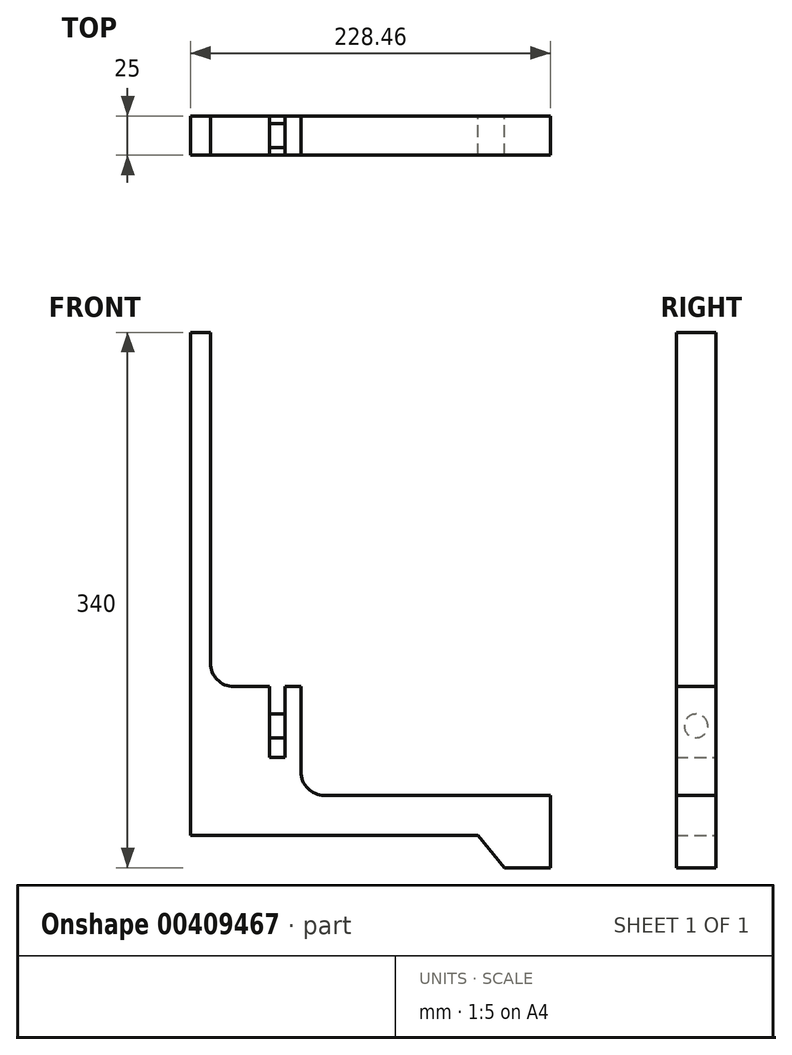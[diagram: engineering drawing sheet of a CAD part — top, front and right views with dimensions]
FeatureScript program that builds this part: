
annotation { "Feature Type Name" : "Feature", "Feature Type Description" : "" }
export const myFeature = defineFeature(function(context is Context, id is Id, definition is map)
    precondition{}
    {
        {
            var Q0;
            Q0=qCreatedBy(makeId("Front.planeOp"),FACE);
            var sketch = newSketch(context, id + "F0", { "sketchPlane" : qUnion([Q0])});
            skLineSegment(sketch, "E0", {"start": v(0, 20.37) * mm, "end": v(0, 340) * mm});
            skLineSegment(sketch, "E1", {"start": v(0, 340) * mm, "end": v(12.5, 340) * mm});
            skLineSegment(sketch, "E2", {"start": v(12.5, 340) * mm, "end": v(12.5, 130) * mm});
            skLineSegment(sketch, "E3", {"start": v(50, 70) * mm, "end": v(60, 70) * mm});
            skLineSegment(sketch, "E4", {"start": v(60, 70) * mm, "end": v(60, 100) * mm});
            skLineSegment(sketch, "E5", {"start": v(60, 100) * mm, "end": v(70, 100) * mm, "construction": true});
            skLineSegment(sketch, "E6", {"start": v(70, 100) * mm, "end": v(70, 60.94) * mm});
            skLineSegment(sketch, "E7", {"start": v(85, 45.94) * mm, "end": v(228.46, 45.94) * mm});
            skLineSegment(sketch, "E8", {"start": v(228.46, 45.94) * mm, "end": v(228.46, 0) * mm});
            skLineSegment(sketch, "E9", {"start": v(228.46, 0) * mm, "end": v(199.18, 0) * mm});
            skLineSegment(sketch, "E10", {"start": v(199.18, 0) * mm, "end": v(182.6, 20.37) * mm});
            skLineSegment(sketch, "E11", {"start": v(182.6, 20.37) * mm, "end": v(0, 20.37) * mm});
            skLineSegment(sketch, "E12", {"start": v(50, 100) * mm, "end": v(50, 70) * mm});
            skLineSegment(sketch, "E13", {"start": v(70, 100) * mm, "end": v(70, 115) * mm});
            skLineSegment(sketch, "E14", {"start": v(70, 115) * mm, "end": v(60, 115) * mm});
            skLineSegment(sketch, "E15", {"start": v(60, 115) * mm, "end": v(60, 100) * mm});
            skLineSegment(sketch, "E16", {"start": v(50, 100) * mm, "end": v(50, 115) * mm});
            skPoint(sketch, "E16.endSnap0", {"position": v(65, 115) * mm});
            skLineSegment(sketch, "E17", {"start": v(50, 115) * mm, "end": v(27.5, 115) * mm});
            skPoint(sketch, "E18.visualSharp", {"position": v(12.5, 115) * mm});
            skArc(sketch, "E18.filletArc", {"start": v(12.5, 130) * mm, "mid": v(16.9, 119.4) * mm, "end": v(27.5, 115) * mm});
            skPoint(sketch, "E19.visualSharp", {"position": v(70, 45.94) * mm});
            skArc(sketch, "E19.filletArc", {"start": v(70, 60.94) * mm, "mid": v(74.4, 50.33) * mm, "end": v(85, 45.94) * mm});
            skSolve(sketch);
        }
        {
            var Q0;
            Q0 = qSketchRegion(id + "F0", true);
            extrude(context, id + "F1", {"entities" : qUnion([Q0]), "depth" : 25 * mm});
        }
        {
            var Q0;
            Q0=makeQuery(id+"F1.opExtrude","SWEPT_FACE",FACE,{"disambiguationData":[OSD([sQuery(id+"F0.wireOp",EDGE,"E6"),sQuery(id+"F0.wireOp",EDGE,"E13")])]});
            var sketch = newSketch(context, id + "F2", { "sketchPlane" : qUnion([Q0])});
            skCircle(sketch, "E20", {"center": v(-12.5, 90) * mm, "radius": 7.5 * mm});
            skPoint(sketch, "E20.centerSnap0", {"position": v(-12.5, 115) * mm});
            skPoint(sketch, "E20.perimeterSnap0", {"position": v(-12.5, 115) * mm});
            skPoint(sketch, "E20.perimeterSnap1", {"position": v(0, 87.97) * mm});
            skSolve(sketch);
        }
        {
            var Q0;
            Q0=makeQuery(id+"F2.imprint","IMPRINT",FACE,{"disambiguationData":[TD([[makeQuery(id+"F2.imprint","IMPRINT",EDGE,{"derivedFrom":sQuery(id+"F2.wireOp",EDGE,"E20")}),1.0]])]});
            extrude(context, id + "F3", {"entities" : qUnion([Q0]), "operationType" : NewBodyOperationType.ADD, "oppositeDirection" : true, "depth" : 56 * mm});
        }
    });
